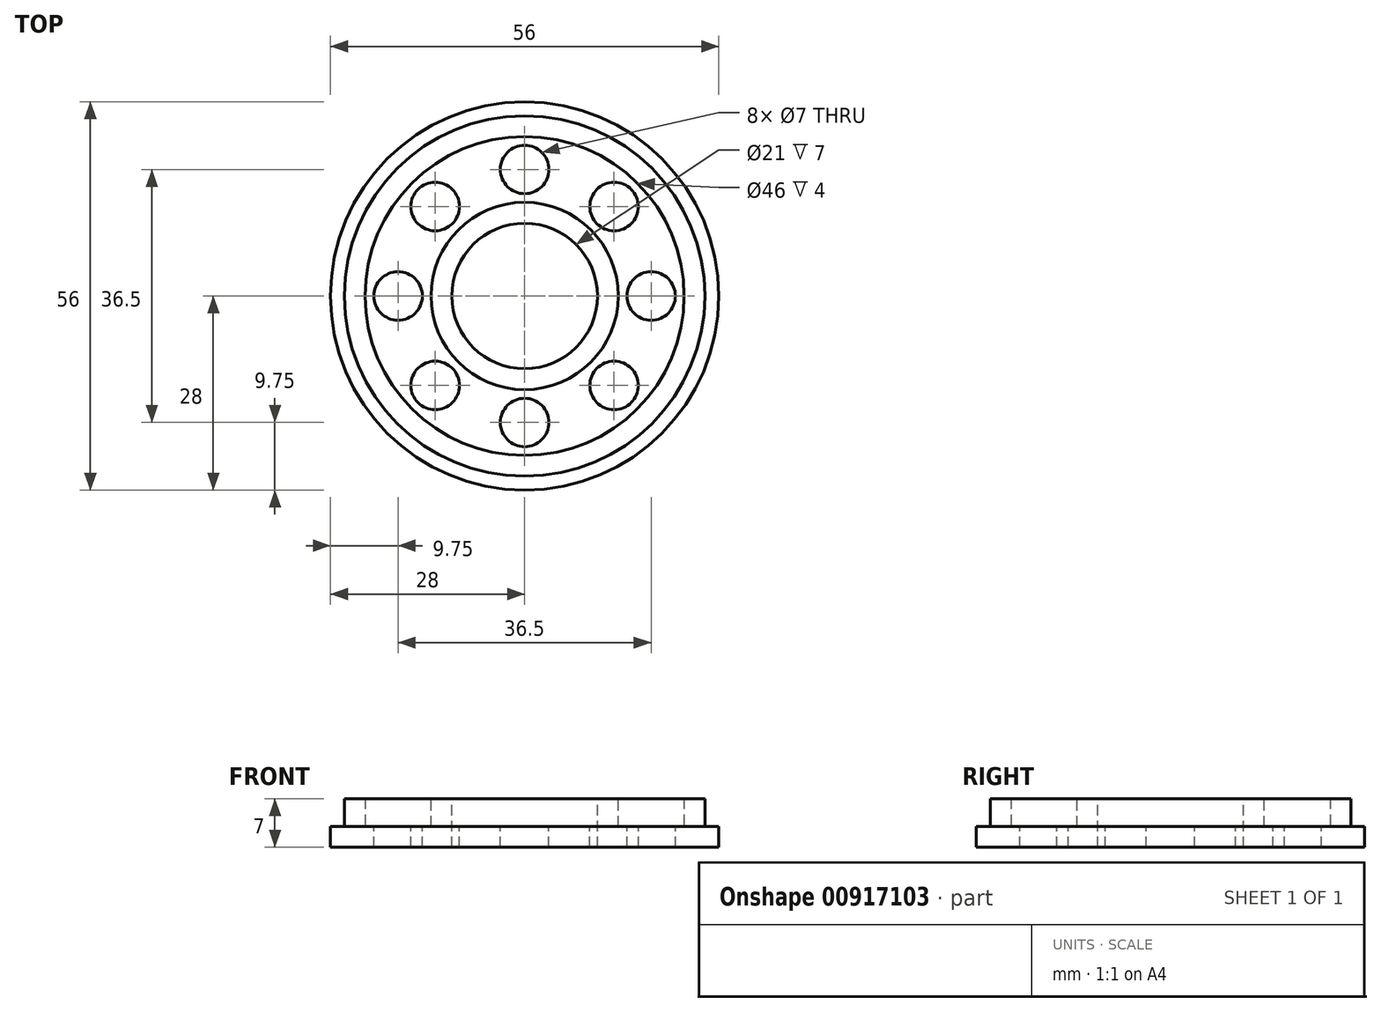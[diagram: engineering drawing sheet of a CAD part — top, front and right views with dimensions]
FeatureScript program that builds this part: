
annotation { "Feature Type Name" : "Feature", "Feature Type Description" : "" }
export const myFeature = defineFeature(function(context is Context, id is Id, definition is map)
    precondition{}
    {
        {
            var Q0;
            Q0=qCreatedBy(makeId("Top.planeOp"),FACE);
            var sketch = newSketch(context, id + "F0", { "sketchPlane" : qUnion([Q0])});
            skCircle(sketch, "E0", {"center": v(0, 0) * mm, "radius": 28 * mm});
            skSolve(sketch);
        }
        {
            var Q0;
            Q0 = qSketchRegion(id + "F0", true);
            extrude(context, id + "F1", {"entities" : qUnion([Q0]), "depth" : 3 * mm, "offsetDistance" : 25.4 * mm});
        }
        {
            var Q0;
            Q0=makeQuery(id+"F1.opExtrude","CAP_FACE",FACE,{"disambiguationData":[OSD([sQuery(id+"F0.wireOp",EDGE,"E0")])],"isStart":false});
            var sketch = newSketch(context, id + "F2", { "sketchPlane" : qUnion([Q0])});
            skCircle(sketch, "E1", {"center": v(0, 0) * mm, "radius": 26 * mm});
            skSolve(sketch);
        }
        {
            var Q0;
            Q0 = qSketchRegion(id + "F2", true);
            extrude(context, id + "F3", {"entities" : qUnion([Q0]), "operationType" : NewBodyOperationType.ADD, "depth" : 4 * mm, "offsetDistance" : 25.4 * mm});
        }
        {
            var Q0;
            Q0=makeQuery(id+"F3.opExtrude","CAP_FACE",FACE,{"disambiguationData":[OSD([sQuery(id+"F2.wireOp",EDGE,"E1")])],"isStart":false});
            var sketch = newSketch(context, id + "F4", { "sketchPlane" : qUnion([Q0])});
            skCircle(sketch, "E2", {"center": v(0, 0) * mm, "radius": 10.5 * mm});
            skSolve(sketch);
        }
        {
            var Q0;
            Q0 = qSketchRegion(id + "F4", true);
            extrude(context, id + "F5", {"entities" : qUnion([Q0]), "operationType" : NewBodyOperationType.REMOVE, "endBound" : BoundingType.THROUGH_ALL, "oppositeDirection" : true, "depth" : 25.4 * mm, "offsetDistance" : 25.4 * mm});
        }
        {
            var Q0;
            Q0=makeQuery(id+"F3.opExtrude","CAP_FACE",FACE,{"disambiguationData":[OSD([sQuery(id+"F2.wireOp",EDGE,"E1")])],"isStart":false});
            shell(context, id + "F6", {"entities" : qUnion([Q0]), "thickness" : 3 * mm});
        }
        {
            var Q0;
            Q0=makeQuery(id+"F6.opShell","OFFSET_FACE",FACE,{"disambiguationData":[OSD([sQuery(id+"F0.wireOp",EDGE,"E0")])]});
            var sketch = newSketch(context, id + "F7", { "sketchPlane" : qUnion([Q0])});
            skCircle(sketch, "E3", {"center": v(-18.25, 0) * mm, "radius": 3.5 * mm});
            skPoint(sketch, "E4.center", {"position": v(0, 0) * mm});
            skCircle(sketch, "E5.1.0", {"center": v(-12.9, -12.9) * mm, "radius": 3.5 * mm});
            skCircle(sketch, "E5.2.0", {"center": v(0, -18.25) * mm, "radius": 3.5 * mm});
            skCircle(sketch, "E5.3.0", {"center": v(12.9, -12.9) * mm, "radius": 3.5 * mm});
            skCircle(sketch, "E5.4.0", {"center": v(18.25, 0) * mm, "radius": 3.5 * mm});
            skCircle(sketch, "E5.5.0", {"center": v(12.9, 12.9) * mm, "radius": 3.5 * mm});
            skCircle(sketch, "E5.6.0", {"center": v(0, 18.25) * mm, "radius": 3.5 * mm});
            skCircle(sketch, "E5.7.0", {"center": v(-12.9, 12.9) * mm, "radius": 3.5 * mm});
            skSolve(sketch);
        }
        {
            var Q0;
            Q0 = qSketchRegion(id + "F7", true);
            extrude(context, id + "F8", {"entities" : qUnion([Q0]), "operationType" : NewBodyOperationType.REMOVE, "endBound" : BoundingType.THROUGH_ALL, "oppositeDirection" : true, "depth" : 25.4 * mm, "offsetDistance" : 25.4 * mm});
        }
    });
